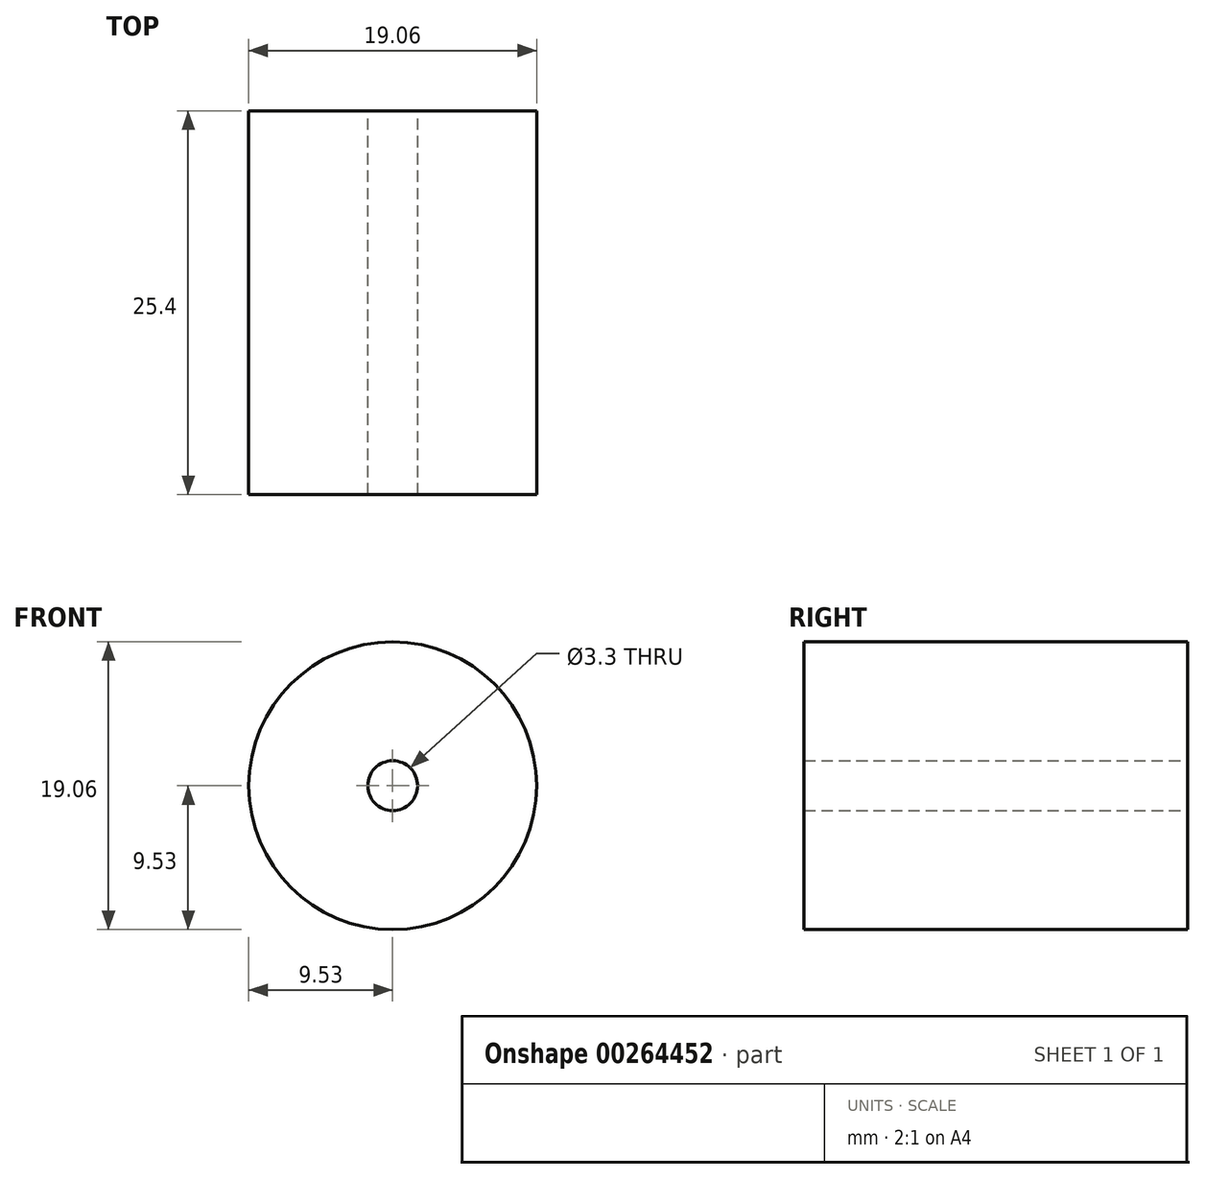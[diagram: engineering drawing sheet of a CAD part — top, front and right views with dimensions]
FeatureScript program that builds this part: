
annotation { "Feature Type Name" : "Feature", "Feature Type Description" : "" }
export const myFeature = defineFeature(function(context is Context, id is Id, definition is map)
    precondition{}
    {
        {
            var Q0;
            Q0=qCreatedBy(makeId("Front.planeOp"),FACE);
            var sketch = newSketch(context, id + "F0", { "sketchPlane" : qUnion([Q0])});
            skCircle(sketch, "E0", {"center": v(0, 0) * mm, "radius": 1.65 * mm});
            skCircle(sketch, "E1", {"center": v(0, 0) * mm, "radius": 9.53 * mm});
            skSolve(sketch);
        }
        {
            var Q0;
            Q0=makeQuery(id+"F0.imprint","IMPRINT",FACE,{"disambiguationData":[TD([[makeQuery(id+"F0.imprint","IMPRINT",EDGE,{"derivedFrom":sQuery(id+"F0.wireOp",EDGE,"E0")}),-1.0]])]});
            extrude(context, id + "F1", {"entities" : qUnion([Q0]), "depth" : 25.4 * mm});
        }
    });
